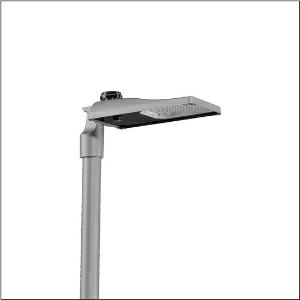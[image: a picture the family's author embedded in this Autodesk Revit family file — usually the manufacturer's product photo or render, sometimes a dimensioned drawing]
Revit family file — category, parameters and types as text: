
# Revit family: streetlight_sl_31_mini___st1_0a_5xh6d35m08ha_c080
name_source: partatom
category: Lighting Fixtures
units: mm (PartAtom-declared; Revit-internal decimal feet)

## family parameters
Cut with Voids When Loaded = No
Host = Face
Light Source = No
Part Type = Normal
Room Calculation Point = No
Round Connector Dimension = Use Diameter
Shared = No

## types (1)
- --- (1 x LED, 9230 lm, 68.2 W, 3000K)
    Apparent Load = 68 VA
    CIE Flux Codes = 37 72 97 100 100
    Color Rendering = 70
    Color Temperature = 3000K
    Default Elevation = 1800 mm
    Description = Streetlight SL 31 mini, mast luminaire, primary light control with lens, of PMMA, primary optical cover: cover, of toughened safety glass, transparent, light distribution: ST1.0a, light emission: direct distribution, primary light characteristic: asymmetric, installation type: post-top, side-entry, LED, High Power LED, rated luminous flux: 9.230lm, luminous efficacy: 135lm/W, light colour: 730, colour temperature: 3000K, control: presetting dimming linear, flexible luminous flux parameterisation, time-dependent luminous flux control, constant luminous flux control, intelligent temperature release in ECG and LED module, overheat protection, with cable H07RN-F 3x 1.5mm², mains connection: 220..240V, AC, 50/60Hz, connection cable pre-assembled, cable length: 8,5m, start of lifetime: 68W, end of service life: 74W, reduction: 30W, luminaire housing, of diecast aluminium, powder-coated, Siteco® metallic grey (DB 702S), corrosivity category C5 high according to DIN EN ISO 12944, no sealing on luminaire upper side, inclination: -15°..+20° (post-top) | -20°..+20° (side-entry), adjustable in 5° steps, mast flange (76/60mm) included as standard, multi-level sealing system, sealing non-destructively replaceable, Smart Interface below, protection rating (complete): IP66, insulation class (complete): insulation class I (protective earthing), certification: CE, ENEC, ENEC+, VDE, UKCA, impact resistance: IK09, permissible operating ambient temperature for outdoor applications: -40..+50°C, standard-compliant lighting for roads and squares, packaging unit: 1 piece

Light Distribution: ST1.0a
    Height = 76 mm
    Lamp = 1 x LED
    Lamp Light Flux = 9230 lm
    Lamp Power = 68.2 W
    Lamp count = 1
    Length = 547 mm
    Luminous efficacy = 135 lm/W
    Manufacturer = Siteco
    ModVariant = No
    Model = 5XH6D35M08HA
    Number of Poles = 1
    OnlyDefault = Yes
    Power Factor = 1
    Product Name = Streetlight SL 31 mini | ST1.0a
    Product group = mast luminaire | pylon top
    ProductGroupID = 6100
    Protection Class = Protection class I
    Protection Degree = IP 66
    RLX_Detail_Level = 1
    RLX_Emergency_Light_Flux = 0 lm
    RLX_Emergency_Type = 0
    RLX_Emergency_Type_DB = No
    RlxData = <blob elided: 40337 chars, md5=4de2585c>
    Socket = socket
    Standby Power = 0 W
    System Light Flux = 9230 lm
    System Power = 68 W
    Type Comments = factory setting: luminous flux: 100 % | dim-lin: 254 | 692 mA
    Type Image = l_1300324.jpg
    URL = http://relux.com
    VarID = @adj_011325
    Voltage = 0 V
    Weight = 0.00 kg
    Width = 265 mm

## geometry (parser evidence)
native form markers: Blend x4, Sweep x10
no freeform markers — native parametric forms only
